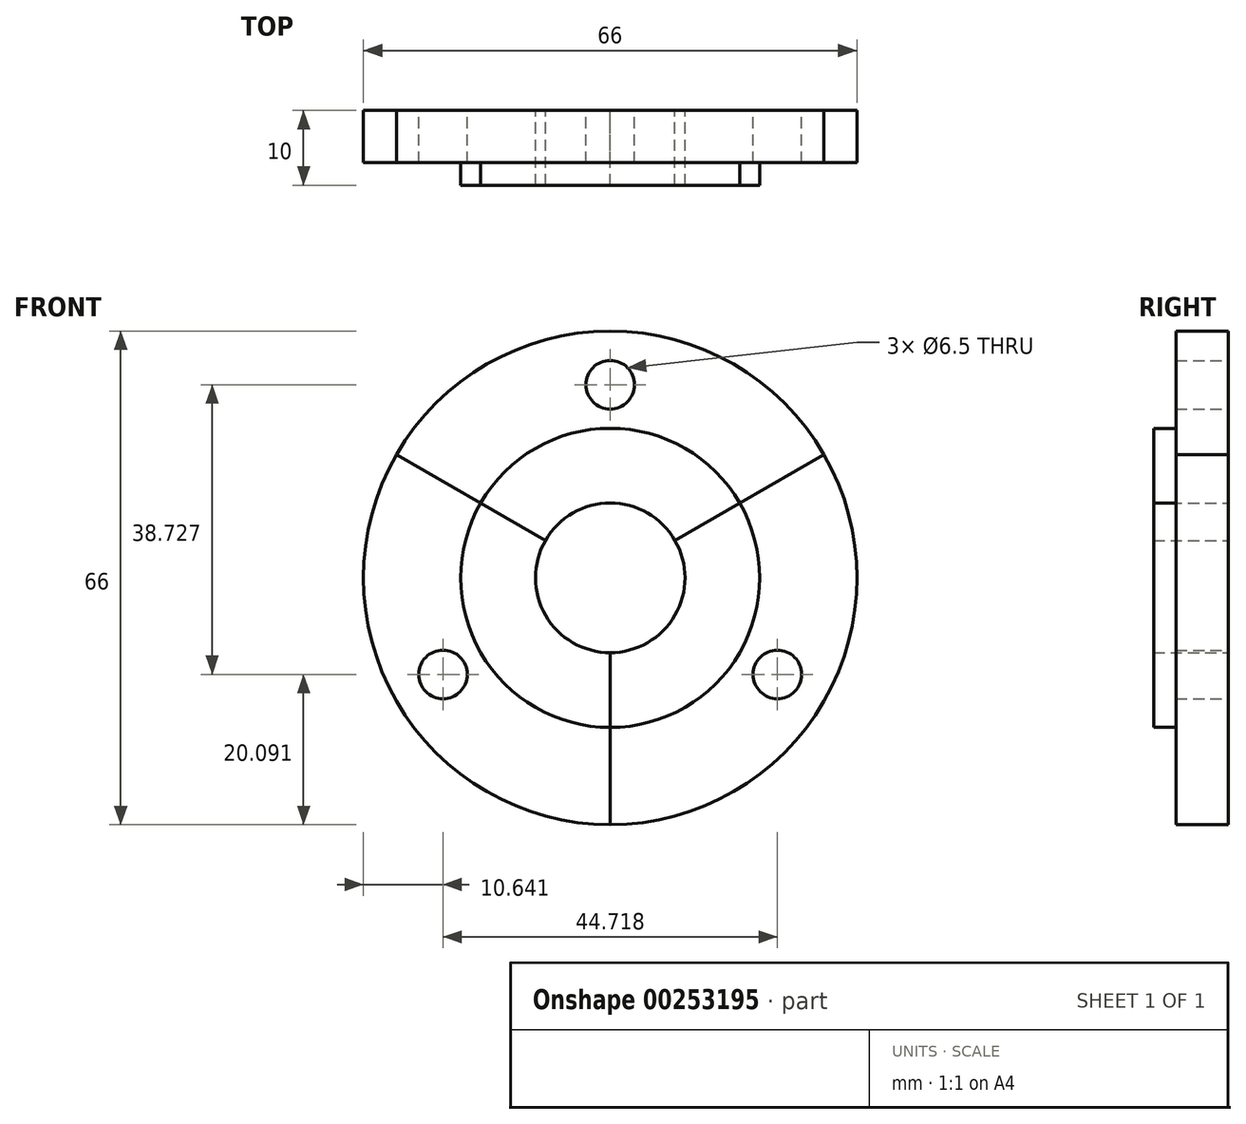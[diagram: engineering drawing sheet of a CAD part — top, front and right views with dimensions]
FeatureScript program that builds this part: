
annotation { "Feature Type Name" : "Feature", "Feature Type Description" : "" }
export const myFeature = defineFeature(function(context is Context, id is Id, definition is map)
    precondition{}
    {
        {
            var Q0;
            Q0=qCreatedBy(makeId("Front.planeOp"),FACE);
            var sketch = newSketch(context, id + "F0", { "sketchPlane" : qUnion([Q0])});
            skCircle(sketch, "E0", {"center": v(0, 0) * mm, "radius": 33 * mm});
            skCircle(sketch, "E1", {"center": v(0, 0) * mm, "radius": 20 * mm});
            skCircle(sketch, "E2", {"center": v(0, 0) * mm, "radius": 10 * mm});
            skLineSegment(sketch, "E3", {"start": v(-28.58, 16.5) * mm, "end": v(0, 0) * mm});
            skLineSegment(sketch, "E4", {"start": v(0, 0) * mm, "end": v(28.58, 16.5) * mm});
            skCircle(sketch, "E5", {"center": v(0, 25.82) * mm, "radius": 3.25 * mm});
            skSolve(sketch);
        }
        {
            var Q0;
            Q0=makeQuery(id+"F0.imprint","IMPRINT",FACE,{"disambiguationData":[TD([[makeQuery(id+"F0.imprint","IMPRINT",EDGE,{"derivedFrom":sQuery(id+"F0.wireOp",EDGE,"E5")}),-1.0]])]});
            extrude(context, id + "F1", {"entities" : qUnion([Q0]), "depth" : 7 * mm});
        }
        {
            var Q0;
            {var subQ0=sQuery(id+"F0.wireOp",EDGE,"E3");var subQ1=sQuery(id+"F0.wireOp",EDGE,"E1");var subQ2=makeQuery(id+"F0.imprint","INTERSECT",VERTEX,{"derivedFrom":[subQ1,subQ0]});Q0=makeQuery(id+"F0.imprint","IMPRINT",FACE,{"disambiguationData":[TD([[makeQuery(id+"F0.imprint","IMPRINT",EDGE,{"disambiguationData":[TD([[subQ2,1.0]])],"derivedFrom":subQ1}),1.0]])]});}
            extrude(context, id + "F2", {"entities" : qUnion([Q0]), "operationType" : NewBodyOperationType.ADD, "depth" : 10 * mm});
        }
        {
            var Q0;
            Q0=makeQuery(id+"F1.opExtrude","SWEPT_BODY",BODY,{"disambiguationData":[OSD([sQuery(id+"F0.wireOp",EDGE,"E0"),sQuery(id+"F0.wireOp",EDGE,"E1"),sQuery(id+"F0.wireOp",EDGE,"E3"),sQuery(id+"F0.wireOp",EDGE,"E4"),sQuery(id+"F0.wireOp",EDGE,"E5")])]});
            var Q1;
            Q1=sQuery(id+"F0.wireOp",EDGE,"E2");
            circularPattern(context, id + "F3", {"entities" : qUnion([Q0]), "axis" : qUnion([Q1]), "angle" : 360 * degree, "instanceCount" : 3, "equalSpace" : true});
        }
    });
